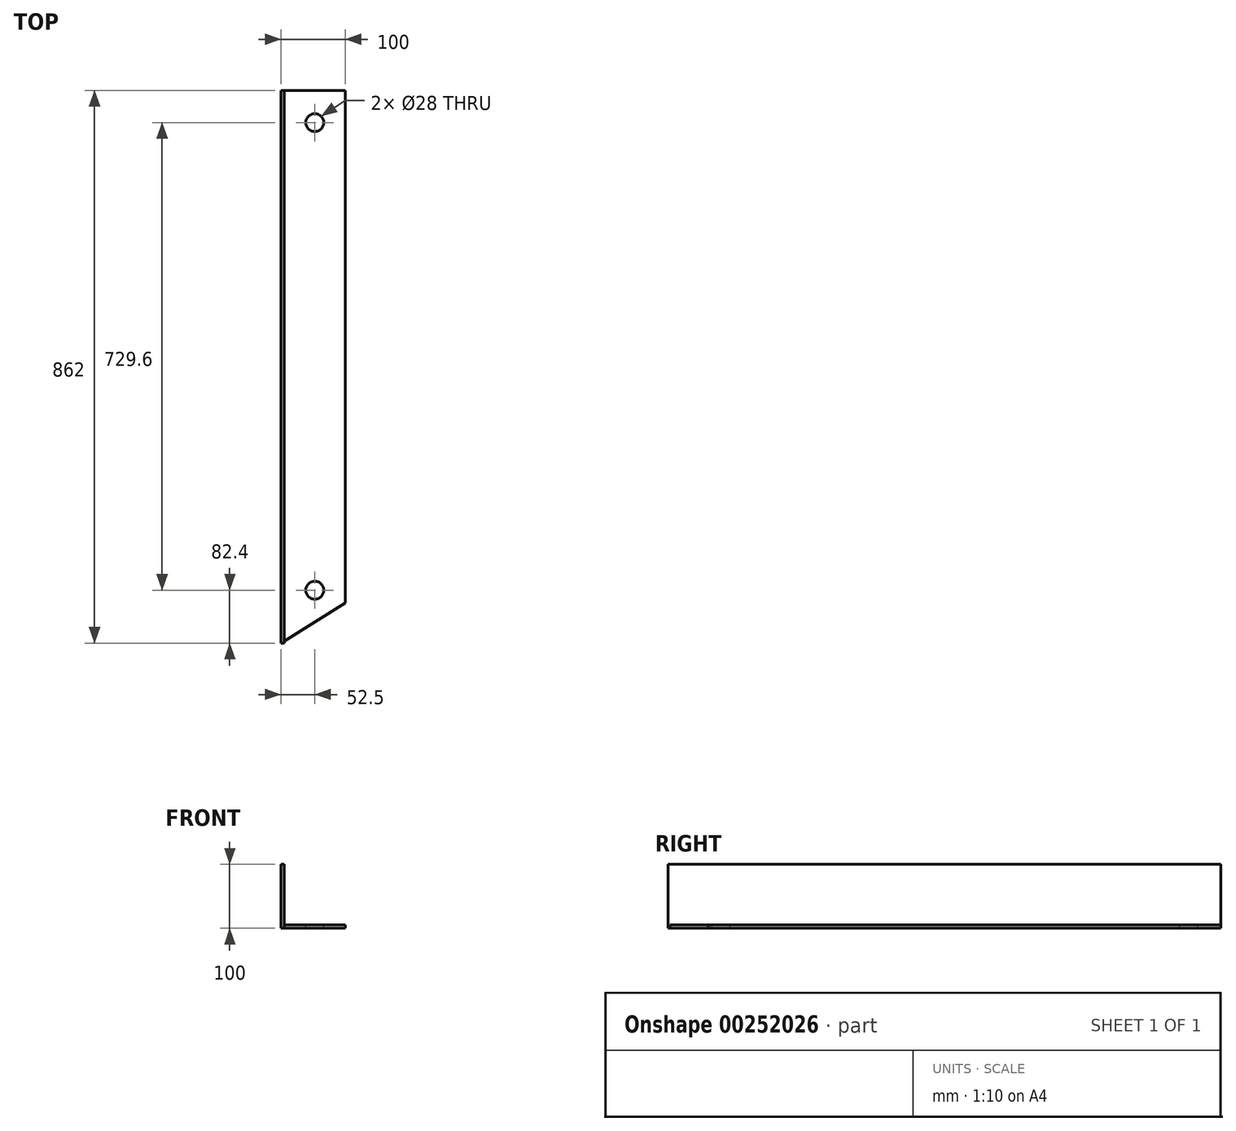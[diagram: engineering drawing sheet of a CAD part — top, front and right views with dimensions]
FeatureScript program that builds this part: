
annotation { "Feature Type Name" : "Feature", "Feature Type Description" : "" }
export const myFeature = defineFeature(function(context is Context, id is Id, definition is map)
    precondition{}
    {
        {
            var Q0;
            Q0=qCreatedBy(makeId("Front.planeOp"),FACE);
            var sketch = newSketch(context, id + "F0", { "sketchPlane" : qUnion([Q0])});
            skLineSegment(sketch, "E0", {"start": v(0, 0) * mm, "end": v(0, 100) * mm});
            skLineSegment(sketch, "E1", {"start": v(0, 100) * mm, "end": v(5, 100) * mm});
            skLineSegment(sketch, "E2", {"start": v(5, 100) * mm, "end": v(5, 5) * mm});
            skLineSegment(sketch, "E3", {"start": v(5, 5) * mm, "end": v(100, 5) * mm});
            skLineSegment(sketch, "E4", {"start": v(100, 5) * mm, "end": v(100, 0) * mm});
            skLineSegment(sketch, "E5", {"start": v(100, 0) * mm, "end": v(0, 0) * mm});
            skSolve(sketch);
        }
        {
            var Q0;
            Q0=makeQuery(id+"F0.imprint","IMPRINT",FACE,{"disambiguationData":[TD([[makeQuery(id+"F0.imprint","IMPRINT",EDGE,{"derivedFrom":sQuery(id+"F0.wireOp",EDGE,"E0")}),-1.0]])]});
            extrude(context, id + "F1", {"entities" : qUnion([Q0]), "depth" : 862 * mm});
        }
        {
            var Q0;
            Q0=makeQuery(id+"F1.opExtrude","SWEPT_FACE",FACE,{"disambiguationData":[OSD([sQuery(id+"F0.wireOp",EDGE,"E3")])]});
            var sketch = newSketch(context, id + "F2", { "sketchPlane" : qUnion([Q0])});
            skCircle(sketch, "E6", {"center": v(52.5, -779.6) * mm, "radius": 14 * mm});
            skCircle(sketch, "E7", {"center": v(52.5, -50) * mm, "radius": 14 * mm});
            skSolve(sketch);
        }
        {
            var Q0;
            Q0=makeQuery(id+"F2.imprint","IMPRINT",FACE,{"disambiguationData":[TD([[makeQuery(id+"F2.imprint","IMPRINT",EDGE,{"derivedFrom":sQuery(id+"F2.wireOp",EDGE,"E7")}),1.0]])]});
            var Q1;
            Q1=makeQuery(id+"F2.imprint","IMPRINT",FACE,{"disambiguationData":[TD([[makeQuery(id+"F2.imprint","IMPRINT",EDGE,{"derivedFrom":sQuery(id+"F2.wireOp",EDGE,"E6")}),1.0]])]});
            var Q2;
            Q2=makeQuery(id+"F1.opExtrude","SWEPT_FACE",FACE,{"disambiguationData":[OSD([sQuery(id+"F0.wireOp",EDGE,"E5")])]});
            extrude(context, id + "F3", {"entities" : qUnion([Q0, Q1]), "operationType" : NewBodyOperationType.REMOVE, "endBound" : BoundingType.UP_TO_SURFACE, "oppositeDirection" : true, "endBoundEntityFace" : qUnion([Q2]), "depth" : 25 * mm});
        }
        {
            var Q0;
            Q0=makeQuery(id+"F2.imprint","IMPRINT",FACE,{"disambiguationData":[TD([[makeQuery(id+"F2.imprint","IMPRINT",EDGE,{"derivedFrom":sQuery(id+"F2.wireOp",EDGE,"E6")}),-1.0]])]});
            var sketch = newSketch(context, id + "F4", { "sketchPlane" : qUnion([Q0])});
            skLineSegment(sketch, "E8", {"start": v(0, -862) * mm, "end": v(110.3, -793.07) * mm});
            skSolve(sketch);
        }
        {
            var Q0;
            {var subQ1=sQuery(id+"F0.wireOp",EDGE,"E3");var subQ6=makeQuery(id+"F2.imprint","IMPRINT",EDGE,{"derivedFrom":makeQuery(id+"F1.opExtrude","CAP_EDGE",EDGE,{"disambiguationData":[OSD([subQ1])],"isStart":false})});Q0=makeQuery(id+"F4.imprint","IMPRINT",FACE,{"disambiguationData":[TD([[makeQuery(id+"F4.imprint","IMPRINT",EDGE,{"derivedFrom":subQ6}),1.0]])]});}
            extrude(context, id + "F5", {"entities" : qUnion([Q0]), "operationType" : NewBodyOperationType.REMOVE, "oppositeDirection" : true, "depth" : 5 * mm});
        }
    });
